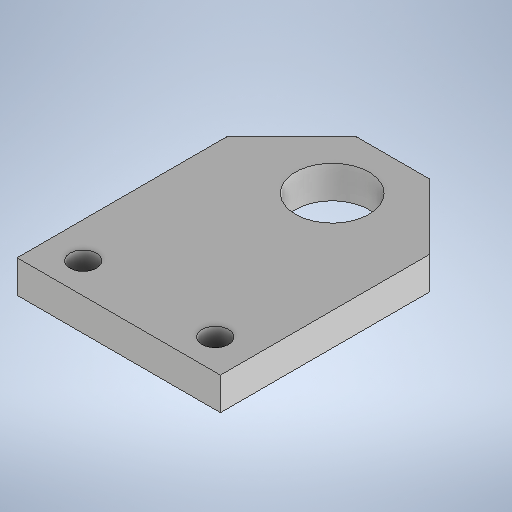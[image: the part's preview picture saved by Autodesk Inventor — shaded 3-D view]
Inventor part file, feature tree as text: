
AUTODESK INVENTOR PART (.ipt)
format: ipt  version: 2025 (Build 290162010, 162A)  size: 276,992 bytes
history: native  units: mm
features: other x2, sheet_metal_op x1, sketch x1
ambient origin geometry x8: Origin, YZ Plane, XZ Plane, XY Plane, X Axis, Y Axis, Z Axis, Center Point
bodies: Solid1 (feature_tree)
feature tree (4):
  sheet_metal_op  "Face1"
  sketch  "Sketch1"  dims[d0=100.0mm d1=36.1mm d2=105.0mm d3=32.0mm d4=135.0mm d6=45.0deg d7=13.0mm d8=65.0mm d9=15.0mm d10=16.0mm]
  other  "Plate1"
  other  "Definition1"
